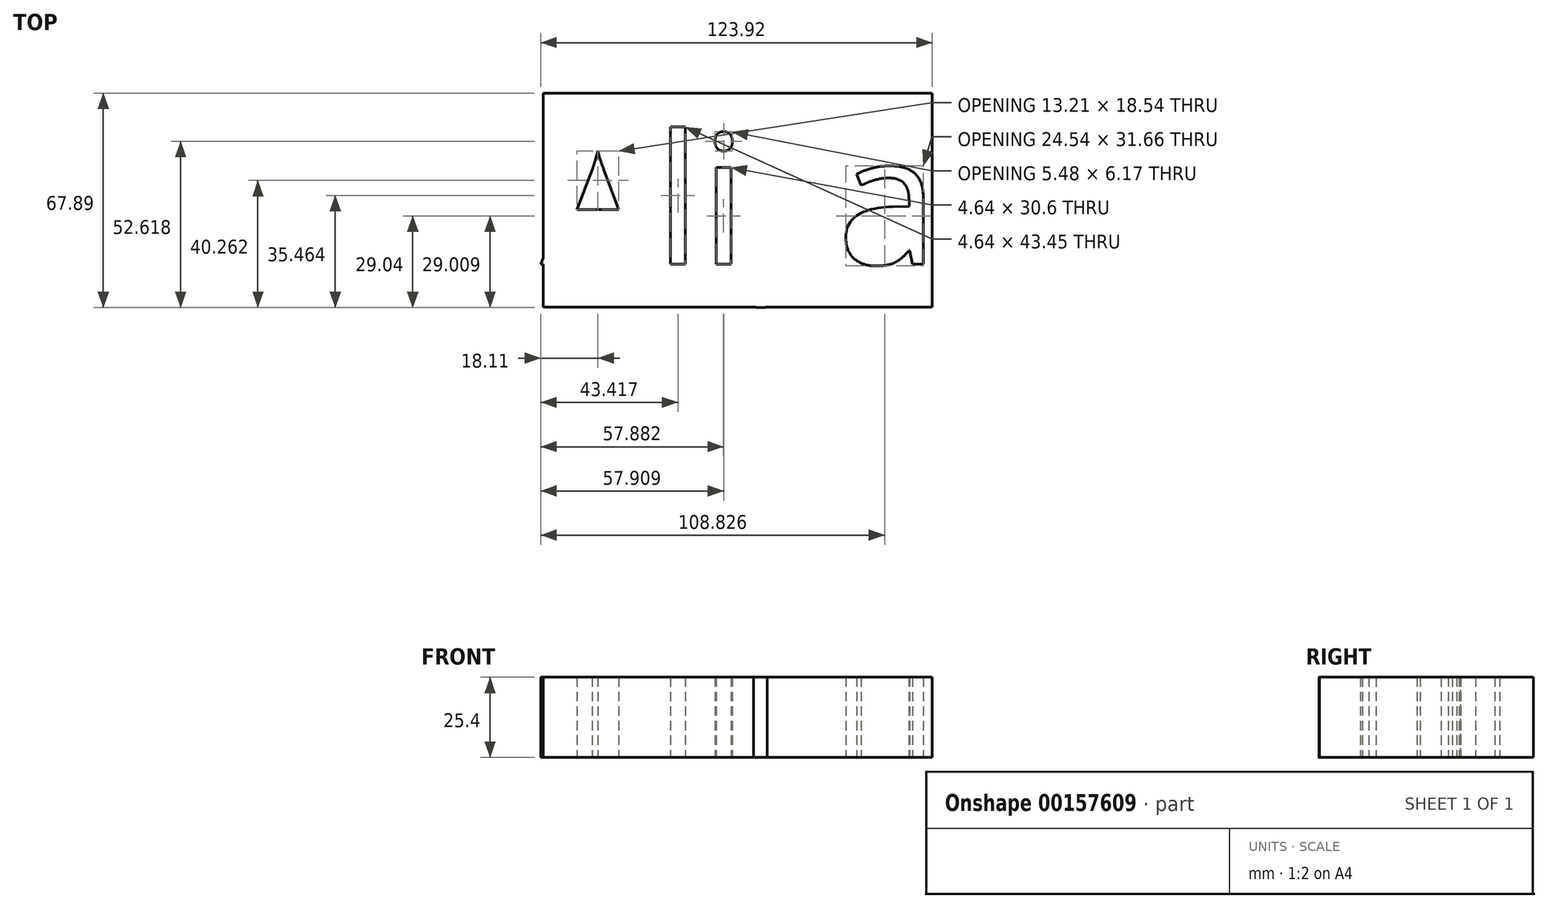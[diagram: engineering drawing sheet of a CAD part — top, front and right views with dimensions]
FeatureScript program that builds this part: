
annotation { "Feature Type Name" : "Feature", "Feature Type Description" : "" }
export const myFeature = defineFeature(function(context is Context, id is Id, definition is map)
    precondition{}
    {
        {
            var Q0;
            Q0=qCreatedBy(makeId("Top.planeOp"),FACE);
            var sketch = newSketch(context, id + "F0", { "sketchPlane" : qUnion([Q0])});
            skLineSegment(sketch, "E0.bottom", {"start": v(-60.03, 37.82) * mm, "end": v(63.08, 37.82) * mm});
            skLineSegment(sketch, "E0.top", {"start": v(-60.03, -29.92) * mm, "end": v(63.08, -29.92) * mm});
            skLineSegment(sketch, "E0.left", {"start": v(-60.03, 37.82) * mm, "end": v(-60.03, -29.92) * mm});
            skLineSegment(sketch, "E0.right", {"start": v(63.08, 37.82) * mm, "end": v(63.08, -29.92) * mm});
            skText(sketch, "E1", { "text": "Aliya", "fontName": "OpenSans-Regular.ttf"});
            const initialGuessF0  = {"E1": [-0.06084, -0.01633, 1, 0, 0.04117]};
            skSetInitialGuess(sketch, initialGuessF0);
            skSolve(sketch);
        }
        {
            var Q0;
            Q0 = qSketchRegion(id + "F0", true);
            extrude(context, id + "F1", {"entities" : qUnion([Q0]), "depth" : 25.4 * mm});
        }
    });
